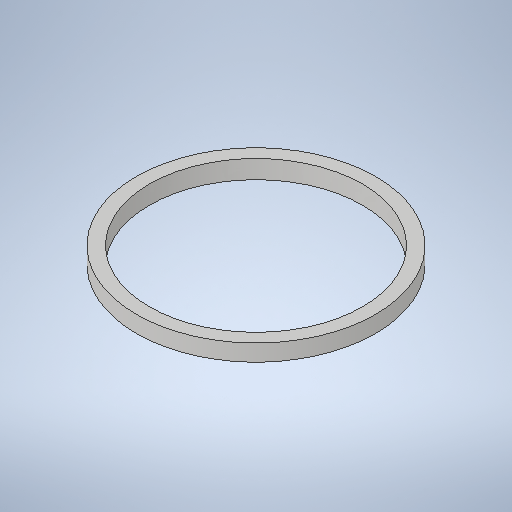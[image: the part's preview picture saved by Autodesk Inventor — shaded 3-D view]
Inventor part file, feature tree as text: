
AUTODESK INVENTOR PART (.ipt)
format: ipt  version: 2025.1 (Build 291241000, 241)  size: 267,776 bytes
history: native  units: mm
features: revolve x1, sketch x1
ambient origin geometry x8: Origin, YZ Plane, XZ Plane, XY Plane, X Axis, Y Axis, Z Axis, Center Point
bodies: 实体1 (feature_tree)
feature tree (2):
  revolve  "旋转1"  [1 undecoded]
  sketch  "草图1"  dims[d0=90.0deg]
note: 1 required parameter value undecoded (feature->parameter linkage not recoverable at this tier; creation-order binding heuristic only, values carry confidence <= 0.55)
